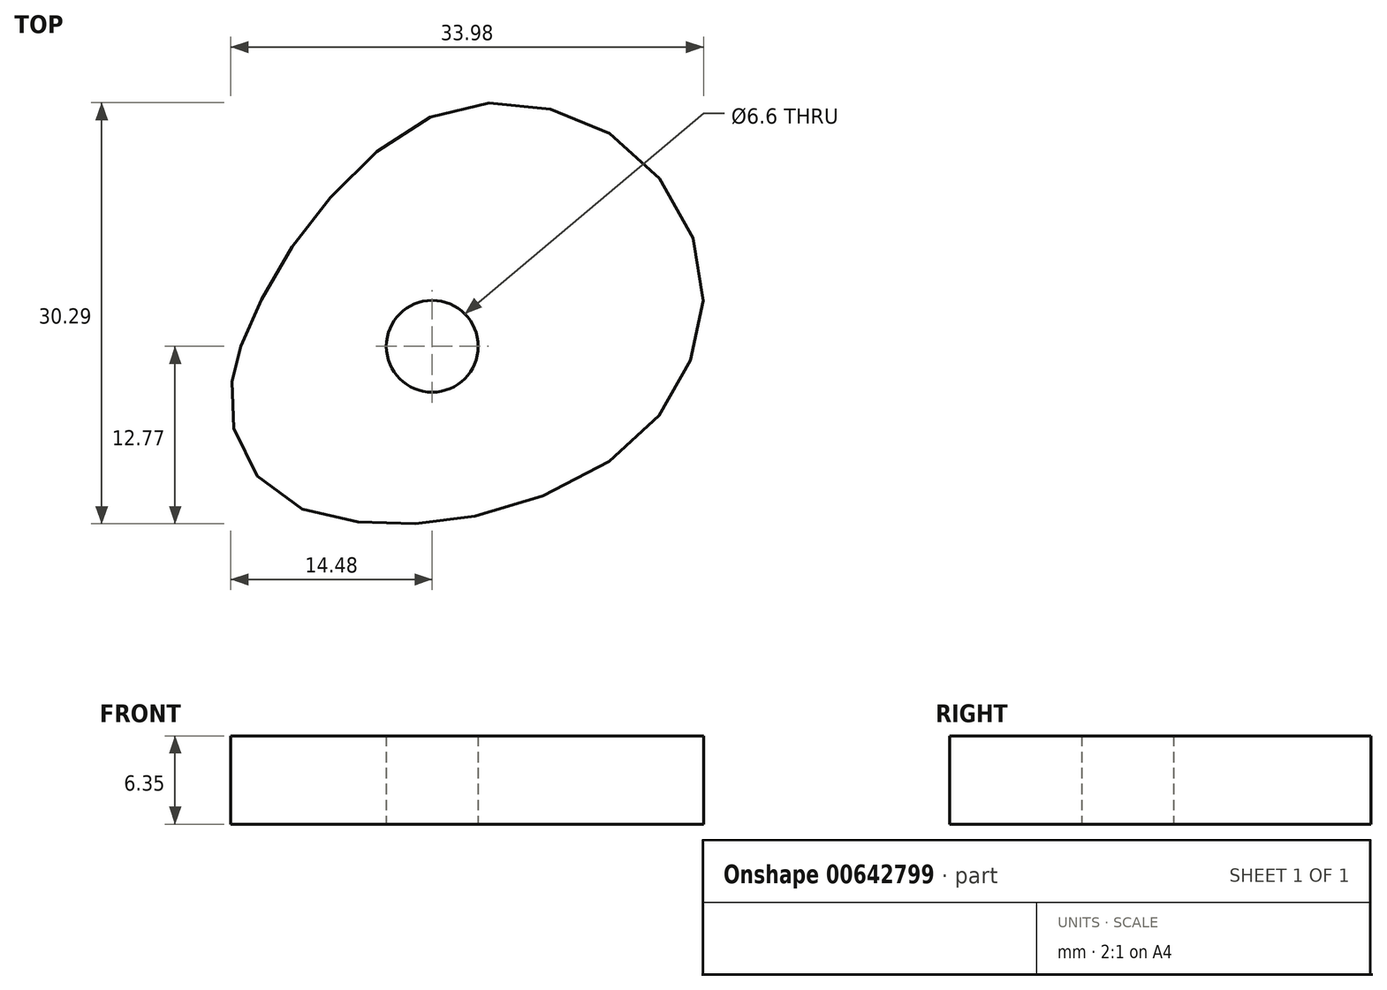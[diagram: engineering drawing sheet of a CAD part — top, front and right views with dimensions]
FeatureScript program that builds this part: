
annotation { "Feature Type Name" : "Feature", "Feature Type Description" : "" }
export const myFeature = defineFeature(function(context is Context, id is Id, definition is map)
    precondition{}
    {
        {
            var Q0;
            Q0=qCreatedBy(makeId("Top.planeOp"),FACE);
            var sketch = newSketch(context, id + "F0", { "sketchPlane" : qUnion([Q0])});
            skFitSpline(sketch, "E0", {"points": [v(-13.77, 0) * mm, v(-14.41, -2.56) * mm, v(-13.9, -7.15) * mm, v(-9.82, -11.48) * mm, v(-3.45, -12.76) * mm, v(3.56, -12.12) * mm, v(13.24, -7.91) * mm, v(18.47, -1.29) * mm, v(19.23, 6.1) * mm, v(14.65, 13.88) * mm, v(7.25, 17.32) * mm, v(0, 16.56) * mm, v(-6.5, 11.59) * mm, v(-11.23, 5.34) * mm, v(-13.77, 0) * mm]});
            skCircle(sketch, "E1", {"center": v(0, 0) * mm, "radius": 3.3 * mm});
            skSolve(sketch);
        }
        {
            var Q0;
            Q0=makeQuery(id+"F0.imprint","IMPRINT",FACE,{"disambiguationData":[TD([[makeQuery(id+"F0.imprint","IMPRINT",EDGE,{"derivedFrom":sQuery(id+"F0.wireOp",EDGE,"E0")}),1.0]])]});
            extrude(context, id + "F1", {"entities" : qUnion([Q0]), "depth" : 6.35 * mm, "offsetDistance" : 25.4 * mm});
        }
    });
